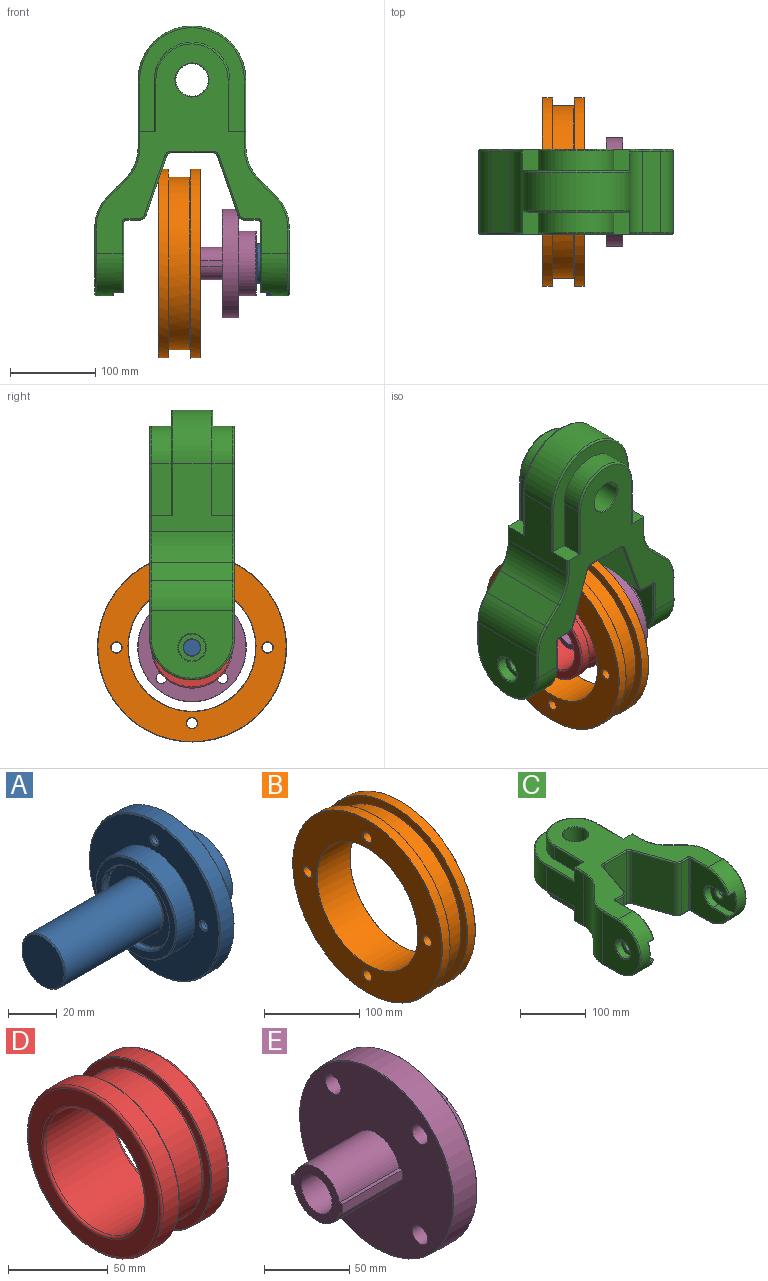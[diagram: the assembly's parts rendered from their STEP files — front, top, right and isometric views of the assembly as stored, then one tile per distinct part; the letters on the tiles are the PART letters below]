
ASSEMBLY  parts=5 mates=7
PART A: 91 faces, bbox 91.6x76.2x76.2 mm
  f0: cylinder r=12.7mm len=56.13mm, axis (-1,0,0), area 4478.7mm2, adj f85,f89
  f1: plane 51.49x51.49mm, normal (1,0,0), area 1010.3mm2, adj f46,f53,f54,f55,f56,f57,f58,f59
  f2: plane 37.59x37.59mm, normal (-1,0,0), area 582.7mm2, adj f85,f86
  f3: plane 7.3x7.3mm, normal (1,0,0), area 29.3mm2, adj f9,f39
  f4: plane 7.3x7.3mm, normal (1,0,0), area 29.3mm2, adj f8,f40
  f5: plane 7.3x7.3mm, normal (1,0,0), area 29.3mm2, adj f6,f41
  f6: cylinder r=2mm len=4mm, axis (-1,0,0), area 22.6mm2, adj f5,f16
  f7: cylinder r=2mm len=4mm, axis (-1,0,0), area 22.6mm2, adj f17,f22
  f8: cylinder r=2mm len=4mm, axis (-1,0,0), area 22.6mm2, adj f4,f15
  f9: cylinder r=2mm len=4mm, axis (-1,0,0), area 22.6mm2, adj f3,f18
  f10: cylinder r=38.1mm len=76.2mm, axis (-1,0,0), area 1829.4mm2, adj f20,f52
  f11: cylinder r=19.05mm len=38.1mm, axis (-1,0,0), area 291.5mm2, adj f19,f86
  f12: plane 75.2x75.2mm, normal (-1,0,0), area 2616.9mm2, adj f13,f15,f16,f17,f18,f20
  f13: cylinder r=23.57mm len=47.15mm, axis (-1,0,0), area 1525mm2, adj f12,f21
  f14: plane 46.15x46.15mm, normal (-1,0,0), area 472mm2, adj f19,f21
  f15: cone r=2mm half-angle=45deg, axis (-1,0,0), area 10mm2, adj f8,f12
  f16: cone r=2mm half-angle=45deg, axis (-1,0,0), area 10mm2, adj f6,f12
  f17: cone r=2mm half-angle=45deg, axis (-1,0,0), area 10mm2, adj f7,f12
  f18: cone r=2mm half-angle=45deg, axis (-1,0,0), area 10mm2, adj f9,f12
  f19: cone r=19.05mm half-angle=45deg, axis (-1,0,0), area 85.7mm2, adj f11,f14
  f20: cone r=37.6mm half-angle=45deg, axis (1,0,0), area 168.2mm2, adj f10,f12
  f21: cone r=23.07mm half-angle=45deg, axis (1,0,0), area 103.6mm2, adj f13,f14
  f22: plane 7.3x7.3mm, normal (1,0,0), area 29.3mm2, adj f7,f42
  f23: cylinder r=3.73mm len=5.84mm, axis (-1,0,0), area 26.7mm2, adj f24,f38,f64,f83
  f24: cylinder r=27.31mm len=16.8mm, axis (-1,0,0), area 143.6mm2, adj f23,f25,f62,f81
  f25: cylinder r=3.73mm len=5.84mm, axis (-1,0,0), area 26.7mm2, adj f24,f26,f60,f79
  f26: cylinder r=6.27mm len=9.73mm, axis (-1,0,0), area 65mm2, adj f25,f27,f58,f77
  f27: cylinder r=3.73mm len=5.84mm, axis (-1,0,0), area 26.7mm2, adj f26,f28,f56,f75
  f28: cylinder r=27.31mm len=16.8mm, axis (-1,0,0), area 143.6mm2, adj f27,f29,f54,f73
  f29: cylinder r=3.73mm len=5.84mm, axis (-1,0,0), area 26.7mm2, adj f28,f30,f53,f71
  f30: cylinder r=6.27mm len=9.73mm, axis (-1,0,0), area 65mm2, adj f29,f31,f55,f69
  f31: cylinder r=3.73mm len=5.84mm, axis (-1,0,0), area 26.7mm2, adj f30,f32,f57,f70
  f32: cylinder r=27.31mm len=16.8mm, axis (-1,0,0), area 143.6mm2, adj f31,f33,f59,f72
  f33: cylinder r=3.73mm len=5.84mm, axis (-1,0,0), area 26.7mm2, adj f32,f34,f61,f74
  f34: cylinder r=6.27mm len=9.73mm, axis (-1,0,0), area 65mm2, adj f33,f35,f63,f76
  f35: cylinder r=3.73mm len=5.84mm, axis (-1,0,0), area 26.7mm2, adj f34,f36,f65,f78
  f36: cylinder r=27.31mm len=16.8mm, axis (-1,0,0), area 143.6mm2, adj f35,f37,f67,f80
  f37: cylinder r=3.73mm len=5.84mm, axis (-1,0,0), area 26.7mm2, adj f36,f38,f68,f82
  f38: cylinder r=6.27mm len=9.73mm, axis (-1,0,0), area 65mm2, adj f23,f37,f66,f84
  f39: cylinder r=3.65mm len=7.3mm, axis (-1,0,0), area 134mm2, adj f3,f49
  f40: cylinder r=3.65mm len=7.3mm, axis (-1,0,0), area 134mm2, adj f4,f50
  f41: cylinder r=3.65mm len=7.3mm, axis (-1,0,0), area 134mm2, adj f5,f47
  f42: cylinder r=3.65mm len=7.3mm, axis (-1,0,0), area 134mm2, adj f22,f48
  f43: plane 75.18x75.18mm, normal (1,0,0), area 2018.3mm2, adj f47,f48,f49,f50,f52,f69,f70,f71
  f44: plane 24.38x24.38mm, normal (-1,0,0), area 467mm2, adj f89
  f45: plane 36.45x36.45mm, normal (1,0,0), area 816mm2, adj f51,f90
  f46: cylinder r=18.73mm len=37.47mm, axis (-1,0,0), area 2855mm2, adj f1,f51
  f47: cone r=3.65mm half-angle=45deg, axis (1,0,0), area 17.6mm2, adj f41,f43
  f48: cone r=3.65mm half-angle=45deg, axis (1,0,0), area 17.6mm2, adj f42,f43
  f49: cone r=3.65mm half-angle=45deg, axis (1,0,0), area 17.6mm2, adj f39,f43
  f50: cone r=3.65mm half-angle=45deg, axis (1,0,0), area 17.6mm2, adj f40,f43
  f51: cone r=18.22mm half-angle=45deg, axis (-1,0,0), area 83.4mm2, adj f45,f46
  f52: cone r=37.59mm half-angle=45deg, axis (-1,0,0), area 170.8mm2, adj f10,f43
  f53: torus R=3.48mm, axis (1,0,0), area 1.8mm2, adj f1,f29,f54,f55
  f54: torus R=27.06mm, axis (1,0,0), area 9.8mm2, adj f1,f28,f53,f56
  f55: torus R=6.52mm, axis (1,0,0), area 4.5mm2, adj f1,f30,f53,f57
  f56: torus R=3.48mm, axis (1,0,0), area 1.8mm2, adj f1,f27,f54,f58
  f57: torus R=3.48mm, axis (1,0,0), area 1.8mm2, adj f1,f31,f55,f59
  f58: torus R=6.52mm, axis (1,0,0), area 4.5mm2, adj f1,f26,f56,f60
  f59: torus R=27.06mm, axis (1,0,0), area 9.8mm2, adj f1,f32,f57,f61
  f60: torus R=3.48mm, axis (1,0,0), area 1.8mm2, adj f1,f25,f58,f62
  f61: torus R=3.48mm, axis (1,0,0), area 1.8mm2, adj f1,f33,f59,f63
  f62: torus R=27.06mm, axis (1,0,0), area 9.8mm2, adj f1,f24,f60,f64
  f63: torus R=6.52mm, axis (1,0,0), area 4.5mm2, adj f1,f34,f61,f65
  f64: torus R=3.48mm, axis (1,0,0), area 1.8mm2, adj f1,f23,f62,f66
  f65: torus R=3.48mm, axis (1,0,0), area 1.8mm2, adj f1,f35,f63,f67
  f66: torus R=6.52mm, axis (1,0,0), area 4.5mm2, adj f1,f38,f64,f68
  f67: torus R=27.06mm, axis (1,0,0), area 9.8mm2, adj f1,f36,f65,f68
  f68: torus R=3.48mm, axis (1,0,0), area 1.8mm2, adj f1,f37,f66,f67
  f69: torus R=6.02mm, axis (1,0,0), area 4.4mm2, adj f30,f43,f70,f71
  f70: torus R=3.98mm, axis (1,0,0), area 1.9mm2, adj f31,f43,f69,f72
  f71: torus R=3.98mm, axis (1,0,0), area 1.9mm2, adj f29,f43,f69,f73
  f72: torus R=27.56mm, axis (1,0,0), area 9.8mm2, adj f32,f43,f70,f74
  f73: torus R=27.56mm, axis (1,0,0), area 9.8mm2, adj f28,f43,f71,f75
  f74: torus R=3.98mm, axis (1,0,0), area 1.9mm2, adj f33,f43,f72,f76
  f75: torus R=3.98mm, axis (1,0,0), area 1.9mm2, adj f27,f43,f73,f77
  f76: torus R=6.02mm, axis (1,0,0), area 4.4mm2, adj f34,f43,f74,f78
  f77: torus R=6.02mm, axis (1,0,0), area 4.4mm2, adj f26,f43,f75,f79
  f78: torus R=3.98mm, axis (1,0,0), area 1.9mm2, adj f35,f43,f76,f80
  f79: torus R=3.98mm, axis (1,0,0), area 1.9mm2, adj f25,f43,f77,f81
  f80: torus R=27.56mm, axis (1,0,0), area 9.8mm2, adj f36,f43,f78,f82
  f81: torus R=27.56mm, axis (1,0,0), area 9.8mm2, adj f24,f43,f79,f83
  f82: torus R=3.98mm, axis (1,0,0), area 1.9mm2, adj f37,f43,f80,f84
  f83: torus R=3.98mm, axis (1,0,0), area 1.9mm2, adj f23,f43,f81,f84
  f84: torus R=6.02mm, axis (1,0,0), area 4.4mm2, adj f38,f43,f82,f83
  f85: torus R=12.95mm, axis (-1,0,0), area 32.1mm2, adj f0,f2
  f86: torus R=18.8mm, axis (-1,0,0), area 47.5mm2, adj f2,f11
  f87: cone r=0mm half-angle=59deg, axis (1,0,0), area 234.6mm2, adj f88
  f88: cylinder r=8mm len=50.41mm, axis (-1,0,0), area 2533.8mm2, adj f87,f90
  f89: cone r=12.7mm half-angle=45deg, axis (1,0,0), area 56.2mm2, adj f0,f44
  f90: cone r=8.51mm half-angle=45deg, axis (1,0,0), area 37.3mm2, adj f45,f88
PART B: 28 faces, bbox 49.5x240.6x240.6 mm
  f0: cylinder r=111.12mm len=222.25mm, axis (-1,0,0), area 7980.6mm2, adj f20,f27
  f1: plane 221.49x221.49mm, normal (-1,0,0), area 20108.4mm2, adj f10,f12,f14,f16,f17,f20
  f2: cylinder r=111.12mm len=222.25mm, axis (-1,0,0), area 7980.6mm2, adj f19,f26
  f3: plane 221.49x221.49mm, normal (1,0,0), area 20108.4mm2, adj f9,f11,f13,f15,f18,f19
  f4: cylinder r=75mm len=150mm, axis (1,0,0), area 22981.4mm2, adj f17,f18
  f5: cylinder r=6.35mm len=48.77mm, axis (1,0,0), area 1945.8mm2, adj f15,f16
  f6: cylinder r=6.35mm len=48.77mm, axis (1,0,0), area 1945.8mm2, adj f13,f14
  f7: cylinder r=6.35mm len=48.77mm, axis (1,0,0), area 1945.8mm2, adj f11,f12
  f8: cylinder r=6.35mm len=48.77mm, axis (1,0,0), area 1945.8mm2, adj f9,f10
  f9: torus R=6.73mm, axis (-1,0,0), area 24.4mm2, adj f3,f8
  f10: torus R=6.73mm, axis (1,0,0), area 24.4mm2, adj f1,f8
  f11: torus R=6.73mm, axis (-1,0,0), area 24.4mm2, adj f3,f7
  f12: torus R=6.73mm, axis (1,0,0), area 24.4mm2, adj f1,f7
  f13: torus R=6.73mm, axis (-1,0,0), area 24.4mm2, adj f3,f6
  f14: torus R=6.73mm, axis (1,0,0), area 24.4mm2, adj f1,f6
  f15: torus R=6.73mm, axis (-1,0,0), area 24.4mm2, adj f3,f5
  f16: torus R=6.73mm, axis (1,0,0), area 24.4mm2, adj f1,f5
  f17: torus R=75.38mm, axis (1,0,0), area 282.5mm2, adj f1,f4
  f18: torus R=75.38mm, axis (-1,0,0), area 282.5mm2, adj f3,f4
  f19: torus R=110.74mm, axis (-1,0,0), area 417.3mm2, adj f2,f3
  f20: torus R=110.74mm, axis (1,0,0), area 417.3mm2, adj f0,f1
  f21: plane 221.74x221.74mm, normal (1,0,0), area 6026mm2, adj f25,f27
  f22: plane 221.74x221.74mm, normal (-1,0,0), area 6026mm2, adj f24,f26
  f23: cylinder r=101.6mm len=203.2mm, axis (-1,0,0), area 15890.3mm2, adj f24,f25
  f24: torus R=101.85mm, axis (1,0,0), area 254.9mm2, adj f22,f23
  f25: torus R=101.85mm, axis (-1,0,0), area 254.9mm2, adj f21,f23
  f26: torus R=110.87mm, axis (1,0,0), area 278.3mm2, adj f2,f22
  f27: torus R=110.87mm, axis (-1,0,0), area 278.3mm2, adj f0,f21
PART C: 147 faces, bbox 237.4x327.3x108.7 mm
  f0: cylinder r=9.53mm len=95.99mm, axis (0,0,-1), area 1131.2mm2, adj f21,f121,f122,f130
  f1: plane 31.75x31.75mm, normal (1,0,0), area 564.5mm2, adj f26,f102
  f2: cylinder r=9.75mm len=19.5mm, axis (1,0,0), area 482.4mm2, adj f99,f100
  f3: plane 95.99x80.47mm, normal (1,0,0), area 5135.7mm2, adj f20,f89,f90,f92,f117,f118,f125,f126
  f4: cylinder r=50mm len=100mm, axis (-1,0,0), area 4264mm2, adj f7,f10,f58,f91,f93,f94,f117,f126
  f5: cylinder r=8mm len=15.99mm, axis (1,0,0), area 395.7mm2, adj f101,f102
  f6: cylinder r=63.5mm len=127mm, axis (0,0,-1), area 9017mm2, adj f8,f9,f45,f48
  f7: plane 246.45x224.6mm, normal (0,0,-1), area 18534.9mm2, adj f4,f25,f36,f37,f41,f42,f43,f59
  f8: plane 96x80mm, normal (1,0,0), area 4615.5mm2, adj f6,f15,f33,f36,f44,f47,f64,f74
  f9: plane 96x80mm, normal (-1,0,0), area 4615.5mm2, adj f6,f16,f32,f37,f46,f49,f53,f63
  f10: plane 246.45x224.6mm, normal (0,0,1), area 18534.9mm2, adj f4,f25,f32,f33,f50,f51,f52,f53
  f11: plane 95.99x80.47mm, normal (-1,0,0), area 5135.7mm2, adj f23,f83,f84,f86,f105,f106,f111,f112
  f12: plane 96x79.12mm, normal (1,0,0), area 5711.6mm2, adj f13,f68,f69,f70,f97
  f13: cylinder r=50.8mm len=96mm, axis (0,0,-1), area 3830.2mm2, adj f12,f14,f67,f71
  f14: plane 96x21.04mm, normal (0.71,0.71,0), area 2856.8mm2, adj f13,f15,f66,f72
  f15: cylinder r=50.8mm len=96mm, axis (0,0,-1), area 3830.2mm2, adj f8,f14,f65,f73
  f16: cylinder r=50.8mm len=96mm, axis (0,0,-1), area 3830.2mm2, adj f9,f17,f54,f62
  f17: plane 96x21.04mm, normal (-0.71,0.71,0), area 2856.8mm2, adj f16,f18,f55,f61
  f18: cylinder r=50.8mm len=96mm, axis (0,0,-1), area 3830.2mm2, adj f17,f19,f56,f60
  f19: plane 96x79.12mm, normal (-1,0,0), area 5711.6mm2, adj f18,f57,f58,f59,f98
  f20: cylinder r=2.03mm len=95.99mm, axis (0,0,-1), area 306.4mm2, adj f3,f21,f119,f124
  f21: plane 95.99x15.19mm, normal (0,-1,0), area 1457.6mm2, adj f0,f20,f120,f123
  f22: plane 95.99x15.19mm, normal (0,-1,0), area 1457.7mm2, adj f23,f103,f108,f114
  f23: cylinder r=2.03mm len=95.99mm, axis (0,0,-1), area 306.4mm2, adj f11,f22,f107,f113
  f24: cylinder r=19.05mm len=98mm, axis (0,0,-1), area 11730.1mm2, adj f95,f96
  f25: cylinder r=50mm len=100mm, axis (-1,0,0), area 4264mm2, adj f7,f10,f69,f85,f87,f88,f105,f111
  f26: cylinder r=15.88mm len=31.75mm, axis (1,0,0), area 1167mm2, adj f1,f97
  f27: plane 31.75x31.75mm, normal (-1,0,0), area 461.2mm2, adj f28,f100
  f28: cylinder r=15.88mm len=31.75mm, axis (-1,0,0), area 1167mm2, adj f27,f98
  f29: plane 60.33x23.4mm, normal (1,0,0), area 1411.6mm2, adj f30,f33,f34,f50
  f30: cylinder r=44.45mm len=88.9mm, axis (0,0,1), area 3267.7mm2, adj f29,f31,f34,f51
  f31: plane 60.33x23.4mm, normal (-1,0,0), area 1411.6mm2, adj f30,f32,f34,f52
  f32: plane 27.4x21.05mm, normal (0,1,0), area 484.7mm2, adj f9,f10,f31,f34,f49,f52,f53
  f33: plane 27.4x21.05mm, normal (0,1,0), area 484.7mm2, adj f8,f10,f29,f34,f47,f50,f64
  f34: plane 123x121.83mm, normal (0,0,1), area 4894.6mm2, adj f29,f30,f31,f32,f33,f47,f48,f49
  f35: plane 60.33x23.4mm, normal (1,0,0), area 1411.6mm2, adj f36,f39,f40,f41
  f36: plane 27.4x21.05mm, normal (0,1,0), area 484.7mm2, adj f7,f8,f35,f40,f41,f44,f74
  f37: plane 27.4x21.05mm, normal (0,1,0), area 484.7mm2, adj f7,f9,f38,f40,f43,f46,f63
  f38: plane 60.33x23.4mm, normal (-1,0,0), area 1411.6mm2, adj f37,f39,f40,f43
  f39: cylinder r=44.45mm len=88.9mm, axis (0,0,-1), area 3267.7mm2, adj f35,f38,f40,f42
  f40: plane 123x121.83mm, normal (0,0,-1), area 4894.6mm2, adj f35,f36,f37,f38,f39,f44,f45,f46
  f41: cylinder r=2mm len=60.33mm, axis (0,1,0), area 189.5mm2, adj f7,f35,f36,f42
  f42: torus R=42.45mm, axis (0,0,1), area 431.5mm2, adj f7,f39,f41,f43
  f43: cylinder r=2mm len=60.33mm, axis (0,-1,0), area 189.5mm2, adj f7,f37,f38,f42
  f44: cylinder r=2mm len=60.33mm, axis (0,-1,0), area 189.5mm2, adj f8,f36,f40,f45
  f45: torus R=61.5mm, axis (0,0,-1), area 619.5mm2, adj f6,f40,f44,f46
  f46: cylinder r=2mm len=60.33mm, axis (0,1,0), area 189.5mm2, adj f9,f37,f40,f45
  f47: cylinder r=2mm len=60.33mm, axis (0,-1,0), area 189.5mm2, adj f8,f33,f34,f48
  f48: torus R=61.5mm, axis (0,0,1), area 619.5mm2, adj f6,f34,f47,f49
  f49: cylinder r=2mm len=60.33mm, axis (0,1,0), area 189.5mm2, adj f9,f32,f34,f48
  f50: cylinder r=2mm len=60.33mm, axis (0,1,0), area 189.5mm2, adj f10,f29,f33,f51
  f51: torus R=42.45mm, axis (0,0,1), area 431.5mm2, adj f10,f30,f50,f52
  f52: cylinder r=2mm len=60.33mm, axis (0,-1,0), area 189.5mm2, adj f10,f31,f32,f51
  f53: cylinder r=2mm len=19.68mm, axis (0,1,0), area 61.8mm2, adj f9,f10,f32,f54
  f54: torus R=52.8mm, axis (0,0,1), area 127.1mm2, adj f10,f16,f53,f55
  f55: cylinder r=2mm len=22.46mm, axis (0.71,0.71,0), area 93.5mm2, adj f10,f17,f54,f56
  f56: torus R=48.8mm, axis (0,0,1), area 123.6mm2, adj f10,f18,f55,f57
  f57: cylinder r=2mm len=31.12mm, axis (0,1,0), area 97.8mm2, adj f10,f19,f56,f58
  f58: torus R=48mm, axis (1,0,0), area 486.3mm2, adj f4,f19,f57,f59
  f59: cylinder r=2mm len=31.12mm, axis (0,-1,0), area 97.8mm2, adj f7,f19,f58,f60
  f60: torus R=48.8mm, axis (0,0,1), area 123.6mm2, adj f7,f18,f59,f61
  f61: cylinder r=2mm len=22.46mm, axis (-0.71,-0.71,0), area 93.5mm2, adj f7,f17,f60,f62
  f62: torus R=52.8mm, axis (0,0,1), area 127.1mm2, adj f7,f16,f61,f63
  f63: cylinder r=2mm len=19.68mm, axis (0,-1,0), area 61.8mm2, adj f7,f9,f37,f62
  f64: cylinder r=2mm len=19.68mm, axis (0,-1,0), area 61.8mm2, adj f8,f10,f33,f65
  f65: torus R=52.8mm, axis (0,0,1), area 127.1mm2, adj f10,f15,f64,f66
  f66: cylinder r=2mm len=22.46mm, axis (0.71,-0.71,0), area 93.5mm2, adj f10,f14,f65,f67
  f67: torus R=48.8mm, axis (0,0,1), area 123.6mm2, adj f10,f13,f66,f68
  f68: cylinder r=2mm len=31.12mm, axis (0,-1,0), area 97.8mm2, adj f10,f12,f67,f69
  f69: torus R=48mm, axis (-1,0,0), area 486.3mm2, adj f12,f25,f68,f70
  f70: cylinder r=2mm len=31.12mm, axis (0,1,0), area 97.8mm2, adj f7,f12,f69,f71
  f71: torus R=48.8mm, axis (0,0,1), area 123.6mm2, adj f7,f13,f70,f72
  f72: cylinder r=2mm len=22.46mm, axis (-0.71,0.71,0), area 93.5mm2, adj f7,f14,f71,f73
  f73: torus R=52.8mm, axis (0,0,1), area 127.1mm2, adj f7,f15,f72,f74
  f74: cylinder r=2mm len=19.68mm, axis (0,1,0), area 61.8mm2, adj f7,f8,f36,f73
  f75: plane 56.15x38.27mm, normal (-1,0,0), area 1708.2mm2, adj f76,f77,f78,f85,f87,f88,f101
  f76: cylinder r=19.05mm len=38.1mm, axis (-1,0,0), area 700.2mm2, adj f75,f77,f78,f84
  f77: plane 32.81x11.7mm, normal (0,0,-1), area 383.6mm2, adj f75,f76,f83,f85,f104
  f78: plane 32.81x11.7mm, normal (0,0,1), area 383.6mm2, adj f75,f76,f86,f88,f110
  f79: plane 56.15x38.27mm, normal (1,0,0), area 1604.8mm2, adj f80,f81,f82,f91,f93,f94,f99
  f80: cylinder r=19.05mm len=38.1mm, axis (1,0,0), area 700.2mm2, adj f79,f81,f82,f90
  f81: plane 32.81x11.7mm, normal (0,0,1), area 383.6mm2, adj f79,f80,f89,f91,f116
  f82: plane 32.81x11.7mm, normal (0,0,-1), area 383.6mm2, adj f79,f80,f92,f94,f127
  f83: cylinder r=1mm len=31.7mm, axis (0,1,0), area 49.8mm2, adj f11,f77,f84,f104
  f84: torus R=20.05mm, axis (1,0,0), area 95.8mm2, adj f11,f76,f83,f86
  f85: cylinder r=1mm len=11.69mm, axis (-1,0,0), area 22.1mm2, adj f25,f75,f77,f87,f104
  f86: cylinder r=1mm len=31.7mm, axis (0,-1,0), area 49.8mm2, adj f11,f78,f84,f110
  f87: torus R=49mm, axis (-1,0,0), area 64.2mm2, adj f25,f75,f85,f88
  f88: cylinder r=1mm len=11.69mm, axis (-1,0,0), area 22.1mm2, adj f25,f75,f78,f87,f110
  f89: cylinder r=1mm len=31.7mm, axis (0,1,0), area 49.8mm2, adj f3,f81,f90,f116
  f90: torus R=20.05mm, axis (-1,0,0), area 95.8mm2, adj f3,f80,f89,f92
  f91: cylinder r=1mm len=11.69mm, axis (-1,0,0), area 22.1mm2, adj f4,f79,f81,f93,f116
  f92: cylinder r=1mm len=31.7mm, axis (0,-1,0), area 49.8mm2, adj f3,f82,f90,f127
  f93: torus R=49mm, axis (1,0,0), area 64.2mm2, adj f4,f79,f91,f94
  f94: cylinder r=1mm len=11.69mm, axis (-1,0,0), area 22.1mm2, adj f4,f79,f82,f93,f127
  f95: torus R=20.05mm, axis (0,0,1), area 191.6mm2, adj f7,f24
  f96: torus R=20.05mm, axis (0,0,1), area 191.6mm2, adj f10,f24
  f97: torus R=16.88mm, axis (-1,0,0), area 160.3mm2, adj f12,f26
  f98: torus R=16.88mm, axis (1,0,0), area 160.3mm2, adj f19,f28
  f99: cone r=10.26mm half-angle=45deg, axis (1,0,0), area 45.2mm2, adj f2,f79
  f100: cone r=10.26mm half-angle=45deg, axis (-1,0,0), area 45.2mm2, adj f2,f27
  f101: cone r=8mm half-angle=45deg, axis (-1,0,0), area 37.2mm2, adj f5,f75
  f102: cone r=8.51mm half-angle=45deg, axis (1,0,0), area 37.2mm2, adj f1,f5
  f103: cylinder r=9.53mm len=95.99mm, axis (0,0,-1), area 1131.2mm2, adj f22,f109,f115,f131
  f104: bspline ~2.73x2.29mm, area 5mm2, adj f77,f83,f85,f105
  f105: torus R=47.99mm, axis (1,0,0), area 177.7mm2, adj f11,f25,f104,f106
  f106: cylinder r=2.01mm len=36.87mm, axis (0,1,0), area 116.2mm2, adj f10,f11,f105,f107
  f107: torus R=4.04mm, axis (0,0,1), area 13.7mm2, adj f10,f23,f106,f108
  f108: cylinder r=2.01mm len=15.19mm, axis (-1,0,0), area 47.9mm2, adj f10,f22,f107,f109
  f109: torus R=7.52mm, axis (0,0,1), area 33mm2, adj f10,f103,f108,f132
  f110: bspline ~2.86x2.38mm, area 5mm2, adj f78,f86,f88,f111
  f111: torus R=47.99mm, axis (1,0,0), area 177.7mm2, adj f11,f25,f110,f112
  f112: cylinder r=2.01mm len=36.87mm, axis (0,-1,0), area 116.2mm2, adj f7,f11,f111,f113
  f113: torus R=4.04mm, axis (0,0,1), area 13.7mm2, adj f7,f23,f112,f114
  f114: cylinder r=2.01mm len=15.19mm, axis (1,0,0), area 47.9mm2, adj f7,f22,f113,f115
  f115: torus R=7.52mm, axis (0,0,1), area 33mm2, adj f7,f103,f114,f133
  f116: bspline ~3.14x2.35mm, area 5mm2, adj f81,f89,f91,f117
  f117: torus R=47.99mm, axis (-1,0,0), area 177.7mm2, adj f3,f4,f116,f118
  f118: cylinder r=2.01mm len=36.87mm, axis (0,-1,0), area 116.2mm2, adj f3,f7,f117,f119
  f119: torus R=4.04mm, axis (0,0,1), area 13.7mm2, adj f7,f20,f118,f120
  f120: cylinder r=2.01mm len=15.19mm, axis (-1,0,0), area 47.9mm2, adj f7,f21,f119,f121
  f121: torus R=7.52mm, axis (0,0,1), area 33mm2, adj f0,f7,f120,f128
  f122: torus R=7.52mm, axis (0,0,1), area 33mm2, adj f0,f10,f123,f129
  f123: cylinder r=2.01mm len=15.19mm, axis (1,0,0), area 47.9mm2, adj f10,f21,f122,f124
  f124: torus R=4.04mm, axis (0,0,1), area 13.7mm2, adj f10,f20,f123,f125
  f125: cylinder r=2.01mm len=36.87mm, axis (0,1,0), area 116.2mm2, adj f3,f10,f124,f126
  f126: torus R=47.99mm, axis (-1,0,0), area 177.7mm2, adj f3,f4,f125,f127
  f127: bspline ~2.9x2.62mm, area 5mm2, adj f82,f92,f94,f126
  f128: plane 2.58x2.43mm, normal (0,-1,0), area 0mm2, adj f7,f121,f141
  f129: plane 2.58x2.43mm, normal (0,-1,0), area 0mm2, adj f10,f122,f142
  f130: plane 95.99x68.75mm, normal (0.94,-0.33,0), area 6984.4mm2, adj f0,f136,f141,f142
  f131: plane 95.99x68.75mm, normal (-0.94,-0.33,0), area 6984.4mm2, adj f103,f135,f137,f146
  f132: plane 2.58x2.43mm, normal (0,-1,0), area 0mm2, adj f10,f109,f146
  f133: plane 2.58x2.43mm, normal (0,-1,0), area 0mm2, adj f7,f115,f137
  f134: plane 95.99x47.94mm, normal (0,-1,0), area 4601.6mm2, adj f135,f136,f139,f144
  f135: cylinder r=6.35mm len=95.99mm, axis (0,0,1), area 754.1mm2, adj f131,f134,f138,f145
  f136: cylinder r=6.35mm len=95.99mm, axis (0,0,1), area 754.1mm2, adj f130,f134,f140,f143
  f137: cylinder r=2.01mm len=70.07mm, axis (0.33,-0.94,0), area 230.4mm2, adj f7,f131,f133,f138
  f138: torus R=8.36mm, axis (0,0,1), area 27.6mm2, adj f7,f135,f137,f139
  f139: cylinder r=2.01mm len=47.94mm, axis (1,0,0), area 151.1mm2, adj f7,f134,f138,f140
  f140: torus R=8.36mm, axis (0,0,1), area 27.6mm2, adj f7,f136,f139,f141
  f141: cylinder r=2.01mm len=70.07mm, axis (0.33,0.94,0), area 230.4mm2, adj f7,f128,f130,f140
  f142: cylinder r=2.01mm len=70.07mm, axis (0.33,0.94,0), area 230.4mm2, adj f10,f129,f130,f143
  f143: torus R=8.36mm, axis (0,0,1), area 27.6mm2, adj f10,f136,f142,f144
  f144: cylinder r=2.01mm len=47.94mm, axis (1,0,0), area 151.1mm2, adj f10,f134,f143,f145
  f145: torus R=8.36mm, axis (0,0,1), area 27.6mm2, adj f10,f135,f144,f146
  f146: cylinder r=2.01mm len=70.07mm, axis (0.33,-0.94,0), area 230.4mm2, adj f10,f131,f132,f145
PART D: 16 faces, bbox 48.8x103.6x103.6 mm
  f0: torus R=46.34mm, axis (-1,0,0), area 711.7mm2, adj f1,f15
  f1: plane 92.69x92.69mm, normal (-1,0,0), area 2517.9mm2, adj f0,f2
  f2: torus R=36.69mm, axis (-1,0,0), area 537.3mm2, adj f1,f3
  f3: cylinder r=35.17mm len=70.34mm, axis (-1,0,0), area 10102.7mm2, adj f2,f4
  f4: torus R=36.69mm, axis (-1,0,0), area 537.3mm2, adj f3,f5
  f5: plane 92.69x92.69mm, normal (1,0,0), area 2517.9mm2, adj f4,f6
  f6: torus R=46.34mm, axis (-1,0,0), area 711.7mm2, adj f5,f7
  f7: cylinder r=47.87mm len=95.74mm, axis (-1,0,0), area 3380.8mm2, adj f6,f8
  f8: torus R=47.36mm, axis (-1,0,0), area 239.1mm2, adj f7,f9
  f9: plane 94.72x94.72mm, normal (-1,0,0), area 1396.8mm2, adj f8,f10
  f10: torus R=42.41mm, axis (-1,0,0), area 211mm2, adj f9,f11
  f11: cylinder r=41.9mm len=83.8mm, axis (-1,0,0), area 5583.5mm2, adj f10,f12
  f12: torus R=42.41mm, axis (-1,0,0), area 211mm2, adj f11,f13
  f13: plane 94.72x94.72mm, normal (1,0,0), area 1396.8mm2, adj f12,f14
  f14: torus R=47.36mm, axis (-1,0,0), area 239.1mm2, adj f13,f15
  f15: cylinder r=47.87mm len=95.74mm, axis (-1,0,0), area 3380.1mm2, adj f0,f14
PART E: 88 faces, bbox 89.5x138.2x138.2 mm
  f0: cylinder r=19.05mm len=49.5mm, axis (1,0,0), area 2627.7mm2, adj f1,f80,f84,f85
  f1: plane 127.15x127.15mm, normal (-1,0,0), area 11018.7mm2, adj f0,f74,f76,f77,f78,f79,f81,f82
  f2: cylinder r=38.1mm len=76.2mm, axis (-1,0,0), area 4742.8mm2, adj f70,f71
  f3: plane 127.15x127.15mm, normal (1,0,0), area 7568.5mm2, adj f70,f75,f76,f77,f78,f79
  f4: plane 75.69x75.69mm, normal (1,0,0), area 1982.6mm2, adj f32,f33,f34,f35,f38,f39,f40,f41
  f5: plane 4x4mm, normal (1,0,0), area 12.6mm2, adj f6
  f6: cylinder r=2mm len=29.5mm, axis (1,0,0), area 370.7mm2, adj f5,f32
  f7: plane 4x4mm, normal (1,0,0), area 12.6mm2, adj f8
  f8: cylinder r=2mm len=29.5mm, axis (1,0,0), area 370.7mm2, adj f7,f35
  f9: plane 4x4mm, normal (1,0,0), area 12.6mm2, adj f10
  f10: cylinder r=2mm len=29.5mm, axis (1,0,0), area 370.7mm2, adj f9,f34
  f11: plane 37.08x37.08mm, normal (1,0,0), area 532mm2, adj f36,f37
  f12: cylinder r=19.05mm len=38.1mm, axis (-1,0,0), area 319.2mm2, adj f13,f36
  f13: plane 54.02x54.02mm, normal (1,0,0), area 1202.8mm2, adj f12,f54,f55,f56,f57,f58,f59,f60
  f14: cylinder r=5mm len=10.29mm, axis (1,0,0), area 62.9mm2, adj f15,f29,f49,f62
  f15: cylinder r=28.57mm len=17.58mm, axis (-1,0,0), area 264.7mm2, adj f14,f16,f47,f60
  f16: cylinder r=5mm len=10.29mm, axis (1,0,0), area 62.9mm2, adj f15,f17,f45,f58
  f17: cylinder r=5mm len=10.29mm, axis (1,0,0), area 91.3mm2, adj f16,f18,f43,f56
  f18: cylinder r=5mm len=10.29mm, axis (1,0,0), area 62.9mm2, adj f17,f19,f41,f54
  f19: cylinder r=28.57mm len=17.58mm, axis (-1,0,0), area 264.7mm2, adj f18,f20,f39,f55
  f20: cylinder r=5mm len=10.29mm, axis (1,0,0), area 62.9mm2, adj f19,f21,f38,f57
  f21: cylinder r=5mm len=10.29mm, axis (1,0,0), area 91.3mm2, adj f20,f22,f40,f59
  f22: cylinder r=5mm len=10.29mm, axis (1,0,0), area 62.9mm2, adj f21,f23,f42,f61
  f23: cylinder r=28.57mm len=17.58mm, axis (-1,0,0), area 264.7mm2, adj f22,f24,f44,f63
  f24: cylinder r=5mm len=10.29mm, axis (1,0,0), area 62.9mm2, adj f23,f25,f46,f65
  f25: cylinder r=5mm len=10.29mm, axis (1,0,0), area 91.3mm2, adj f24,f26,f48,f67
  f26: cylinder r=5mm len=10.29mm, axis (1,0,0), area 62.9mm2, adj f25,f27,f50,f69
  f27: cylinder r=28.57mm len=17.58mm, axis (-1,0,0), area 264.7mm2, adj f26,f28,f52,f68
  f28: cylinder r=5mm len=10.29mm, axis (1,0,0), area 62.9mm2, adj f27,f29,f53,f66
  f29: cylinder r=5mm len=10.29mm, axis (1,0,0), area 91.3mm2, adj f14,f28,f51,f64
  f30: plane 4x4mm, normal (1,0,0), area 12.6mm2, adj f31
  f31: cylinder r=2mm len=29.5mm, axis (1,0,0), area 370.7mm2, adj f30,f33
  f32: cone r=2mm half-angle=45deg, axis (1,0,0), area 10.2mm2, adj f4,f6
  f33: cone r=2mm half-angle=45deg, axis (1,0,0), area 10.2mm2, adj f4,f31
  f34: cone r=2mm half-angle=45deg, axis (1,0,0), area 10.2mm2, adj f4,f10
  f35: cone r=2mm half-angle=45deg, axis (1,0,0), area 10.2mm2, adj f4,f8
  f36: cone r=18.54mm half-angle=45deg, axis (-1,0,0), area 84.8mm2, adj f11,f12
  f37: cone r=13.21mm half-angle=45deg, axis (1,0,0), area 58.5mm2, adj f11,f72
  f38: torus R=5.25mm, axis (-1,0,0), area 2.5mm2, adj f4,f20,f39,f40
  f39: torus R=28.83mm, axis (-1,0,0), area 10.3mm2, adj f4,f19,f38,f41
  f40: torus R=4.75mm, axis (-1,0,0), area 3.5mm2, adj f4,f21,f38,f42
  f41: torus R=5.25mm, axis (-1,0,0), area 2.5mm2, adj f4,f18,f39,f43
  f42: torus R=5.25mm, axis (-1,0,0), area 2.5mm2, adj f4,f22,f40,f44
  f43: torus R=4.75mm, axis (-1,0,0), area 3.5mm2, adj f4,f17,f41,f45
  f44: torus R=28.83mm, axis (-1,0,0), area 10.3mm2, adj f4,f23,f42,f46
  f45: torus R=5.25mm, axis (-1,0,0), area 2.5mm2, adj f4,f16,f43,f47
  f46: torus R=5.25mm, axis (-1,0,0), area 2.5mm2, adj f4,f24,f44,f48
  f47: torus R=28.83mm, axis (-1,0,0), area 10.3mm2, adj f4,f15,f45,f49
  f48: torus R=4.75mm, axis (-1,0,0), area 3.5mm2, adj f4,f25,f46,f50
  f49: torus R=5.25mm, axis (-1,0,0), area 2.5mm2, adj f4,f14,f47,f51
  f50: torus R=5.25mm, axis (-1,0,0), area 2.5mm2, adj f4,f26,f48,f52
  f51: torus R=4.75mm, axis (-1,0,0), area 3.5mm2, adj f4,f29,f49,f53
  f52: torus R=28.83mm, axis (-1,0,0), area 10.3mm2, adj f4,f27,f50,f53
  f53: torus R=5.25mm, axis (-1,0,0), area 2.5mm2, adj f4,f28,f51,f52
  f54: torus R=4.75mm, axis (-1,0,0), area 2.4mm2, adj f13,f18,f55,f56
  f55: torus R=28.32mm, axis (-1,0,0), area 10.2mm2, adj f13,f19,f54,f57
  f56: torus R=5.25mm, axis (-1,0,0), area 3.6mm2, adj f13,f17,f54,f58
  f57: torus R=4.75mm, axis (-1,0,0), area 2.4mm2, adj f13,f20,f55,f59
  f58: torus R=4.75mm, axis (-1,0,0), area 2.4mm2, adj f13,f16,f56,f60
  f59: torus R=5.25mm, axis (-1,0,0), area 3.6mm2, adj f13,f21,f57,f61
  f60: torus R=28.32mm, axis (-1,0,0), area 10.2mm2, adj f13,f15,f58,f62
  f61: torus R=4.75mm, axis (-1,0,0), area 2.4mm2, adj f13,f22,f59,f63
  f62: torus R=4.75mm, axis (-1,0,0), area 2.4mm2, adj f13,f14,f60,f64
  f63: torus R=28.32mm, axis (-1,0,0), area 10.2mm2, adj f13,f23,f61,f65
  f64: torus R=5.25mm, axis (-1,0,0), area 3.6mm2, adj f13,f29,f62,f66
  f65: torus R=4.75mm, axis (-1,0,0), area 2.4mm2, adj f13,f24,f63,f67
  f66: torus R=4.75mm, axis (-1,0,0), area 2.4mm2, adj f13,f28,f64,f68
  f67: torus R=5.25mm, axis (-1,0,0), area 3.6mm2, adj f13,f25,f65,f69
  f68: torus R=28.32mm, axis (-1,0,0), area 10.2mm2, adj f13,f27,f66,f69
  f69: torus R=4.75mm, axis (-1,0,0), area 2.4mm2, adj f13,f26,f67,f68
  f70: torus R=38.35mm, axis (-1,0,0), area 95.7mm2, adj f2,f3
  f71: torus R=37.85mm, axis (-1,0,0), area 95.3mm2, adj f2,f4
  f72: cylinder r=12.7mm len=81.39mm, axis (-1,0,0), area 6494.6mm2, adj f37,f80
  f73: cylinder r=63.83mm len=127.65mm, axis (-1,0,0), area 7693.7mm2, adj f74,f75
  f74: torus R=63.57mm, axis (-1,0,0), area 159.8mm2, adj f1,f73
  f75: torus R=63.57mm, axis (-1,0,0), area 159.8mm2, adj f3,f73
  f76: cylinder r=6.35mm len=19.69mm, axis (1,0,0), area 785.7mm2, adj f1,f3
  f77: cylinder r=6.35mm len=19.69mm, axis (1,0,0), area 785.7mm2, adj f1,f3
  f78: cylinder r=6.35mm len=19.69mm, axis (1,0,0), area 785.7mm2, adj f1,f3
  f79: cylinder r=6.35mm len=19.69mm, axis (1,0,0), area 785.7mm2, adj f1,f3
  f80: plane 42.52x38.1mm, normal (-1,0,0), area 664.5mm2, adj f0,f72,f81,f82,f83,f84,f85,f86
  f81: cylinder r=19.05mm len=49.5mm, axis (1,0,0), area 2627.7mm2, adj f1,f80,f82,f87
  f82: plane 49.5x2.51mm, normal (0,0,-1), area 124.1mm2, adj f1,f80,f81,f83
  f83: plane 49.5x6.73mm, normal (0,1,0), area 333.2mm2, adj f1,f80,f82,f84
  f84: plane 49.5x2.51mm, normal (0,0,1), area 124.1mm2, adj f0,f1,f80,f83
  f85: plane 49.5x2.51mm, normal (0,0,1), area 124.1mm2, adj f0,f1,f80,f86
  f86: plane 49.5x6.73mm, normal (0,-1,0), area 333.2mm2, adj f1,f80,f85,f87
  f87: plane 49.5x2.51mm, normal (0,0,-1), area 124.1mm2, adj f1,f80,f81,f86
PLACE A t=(-648.23,506.15,-201.89)mm
PLACE B t=(-25.45,506.15,-201.89)mm
PLACE C rot(axis=(1,0,0),90deg) t=(-10.61,506.15,-456.23)mm
PLACE D rot(axis=(-0.73,-0.18,-0.66),0deg) t=(-406.07,506.15,-201.89)mm
PLACE E t=(-525.96,506.15,-201.89)mm
MATE cylindrical D.f0 <-> E.f0  axis (1,0,0) through (69.16,506.15,-201.89)mm
MATE slider A.f0 <-> C.f2  axis (1,0,0) through (173.54,506.15,-201.89)mm
MATE planar D.f0 <-> B.f8  axis (1,0,0) through (69.16,506.15,-201.89)mm
MATE cylindrical B.f0 <-> E.f0  axis (1,0,0) through (68.78,506.15,-201.89)mm
MATE planar B.f0 <-> E.f0  axis (1,0,0) through (69.16,506.15,-201.89)mm
MATE cylindrical E.f0 <-> A.f0  axis (1,0,0) through (126.45,506.15,-201.89)mm
MATE cylindrical A.f0 <-> C.f2  axis (-1,0,0) through (110.55,506.15,-201.89)mm
